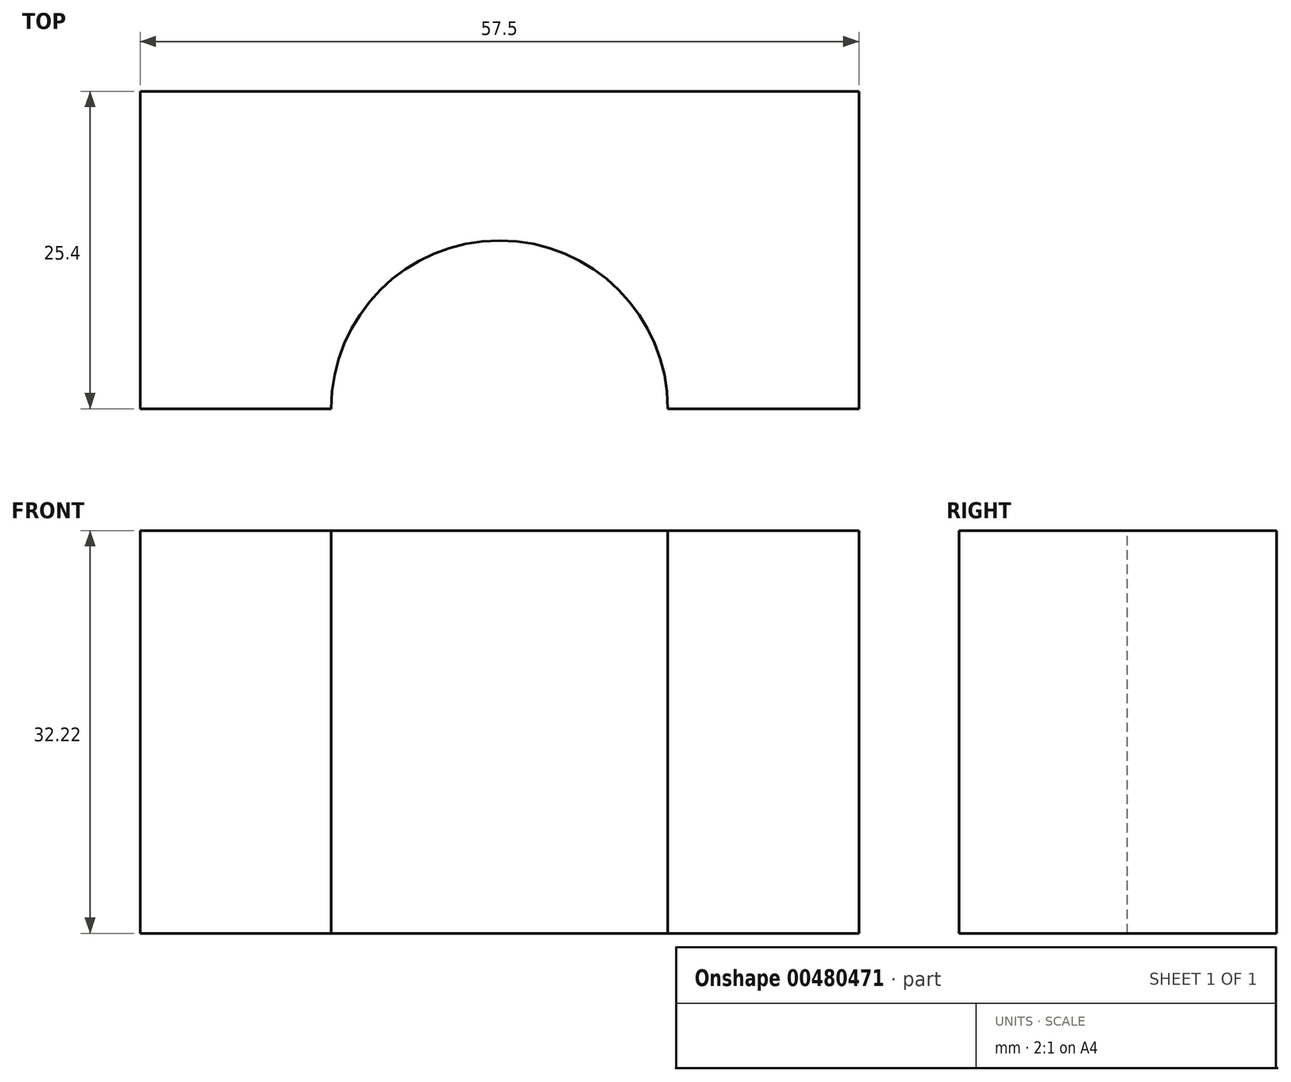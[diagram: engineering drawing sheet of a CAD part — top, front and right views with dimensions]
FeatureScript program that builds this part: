
annotation { "Feature Type Name" : "Feature", "Feature Type Description" : "" }
export const myFeature = defineFeature(function(context is Context, id is Id, definition is map)
    precondition{}
    {
        {
            var Q0;
            Q0=qCreatedBy(makeId("Front.planeOp"),FACE);
            var sketch = newSketch(context, id + "F0", { "sketchPlane" : qUnion([Q0])});
            skLineSegment(sketch, "E0.bottom", {"start": v(28.75, -16.1) * mm, "end": v(-28.75, -16.1) * mm});
            skLineSegment(sketch, "E0.top", {"start": v(28.75, 16.1) * mm, "end": v(-28.75, 16.1) * mm});
            skLineSegment(sketch, "E0.left", {"start": v(28.75, -16.1) * mm, "end": v(28.75, 16.1) * mm});
            skLineSegment(sketch, "E0.right", {"start": v(-28.75, -16.1) * mm, "end": v(-28.75, 16.1) * mm});
            skPoint(sketch, "E0.middle", {"position": v(0, 0) * mm});
            skSolve(sketch);
        }
        {
            var Q0;
            Q0=makeQuery(id+"F0.imprint","IMPRINT",FACE,{"disambiguationData":[TD([[makeQuery(id+"F0.imprint","IMPRINT",EDGE,{"derivedFrom":sQuery(id+"F0.wireOp",EDGE,"E0.bottom")}),-1.0]])]});
            extrude(context, id + "F1", {"entities" : qUnion([Q0]), "depth" : 25.4 * mm});
        }
        {
            var Q0;
            Q0=makeQuery(id+"F1.opExtrude","SWEPT_FACE",FACE,{"disambiguationData":[OSD([sQuery(id+"F0.wireOp",EDGE,"E0.top")])]});
            var sketch = newSketch(context, id + "F2", { "sketchPlane" : qUnion([Q0])});
            skArc(sketch, "E1", {"start": v(13.46, -25.4) * mm, "mid": v(0, -11.94) * mm, "end": v(-13.46, -25.4) * mm});
            skLineSegment(sketch, "E2", {"start": v(-13.46, -25.4) * mm, "end": v(13.46, -25.4) * mm});
            skSolve(sketch);
        }
        {
            var Q0;
            {var subQ0=sQuery(id+"F2.wireOp",EDGE,"E1");var subQ1=makeQuery(id+"F1.opExtrude","CAP_EDGE",EDGE,{"disambiguationData":[OSD([sQuery(id+"F0.wireOp",EDGE,"E0.top")])],"isStart":false});var subQ2=makeQuery(id+"F2.imprint","INTERSECT",VERTEX,{"disambiguationData":[OD(0.0)],"derivedFrom":[subQ1,subQ0]});Q0=makeQuery(id+"F2.imprint","IMPRINT",FACE,{"disambiguationData":[TD([[makeQuery(id+"F2.imprint","IMPRINT",EDGE,{"disambiguationData":[TD([[subQ2,1.0]])],"derivedFrom":subQ0}),1.0]])]});}
            extrude(context, id + "F3", {"entities" : qUnion([Q0]), "operationType" : NewBodyOperationType.REMOVE, "endBound" : BoundingType.THROUGH_ALL, "oppositeDirection" : true, "depth" : 25.4 * mm});
        }
    });
